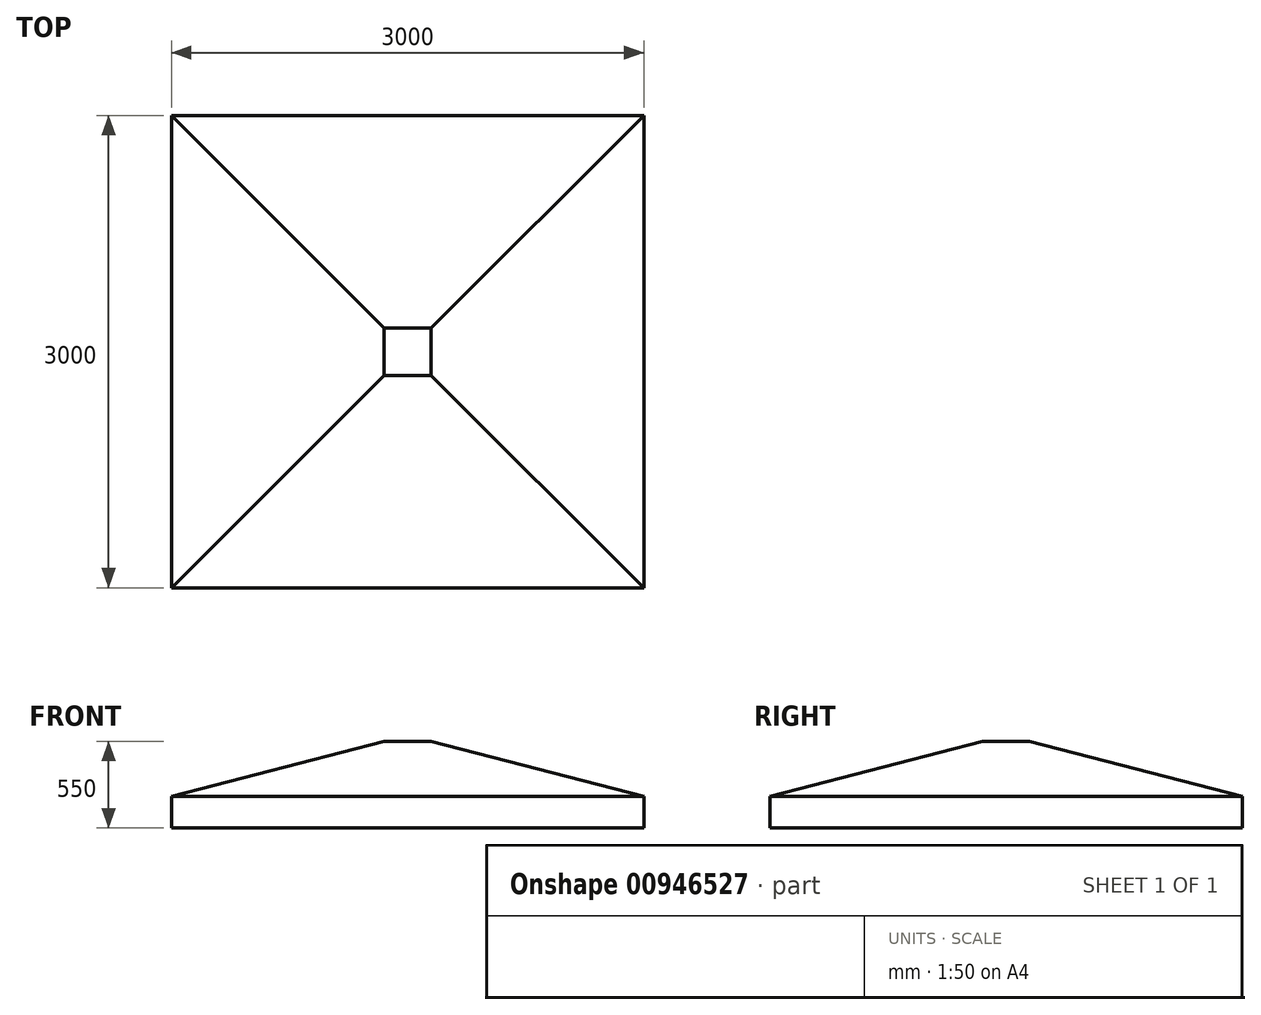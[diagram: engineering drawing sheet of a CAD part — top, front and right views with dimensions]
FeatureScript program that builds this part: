
annotation { "Feature Type Name" : "Feature", "Feature Type Description" : "" }
export const myFeature = defineFeature(function(context is Context, id is Id, definition is map)
    precondition{}
    {
        {
            var Q0;
            Q0=qCreatedBy(makeId("Top.planeOp"),FACE);
            cPlane(context, id + "F0", {"entities" : qUnion([Q0]), "cplaneType" : CPlaneType.OFFSET, "offset" : 350 * mm, "width" : 150 * mm, "height" : 150 * mm});
        }
        {
            var Q0;
            Q0=qCreatedBy(id+"F0.planeOp",FACE);
            var sketch = newSketch(context, id + "F1", { "sketchPlane" : qUnion([Q0])});
            skLineSegment(sketch, "E0.bottom", {"start": v(150, -150) * mm, "end": v(-150, -150) * mm});
            skLineSegment(sketch, "E0.top", {"start": v(150, 150) * mm, "end": v(-150, 150) * mm});
            skLineSegment(sketch, "E0.left", {"start": v(150, -150) * mm, "end": v(150, 150) * mm});
            skLineSegment(sketch, "E0.right", {"start": v(-150, -150) * mm, "end": v(-150, 150) * mm});
            skPoint(sketch, "E0.middle", {"position": v(0, 0) * mm});
            skSolve(sketch);
        }
        {
            var Q0;
            Q0=qCreatedBy(makeId("Top.planeOp"),FACE);
            var sketch = newSketch(context, id + "F2", { "sketchPlane" : qUnion([Q0])});
            skLineSegment(sketch, "E1.bottom", {"start": v(1500, -1500) * mm, "end": v(-1500, -1500) * mm});
            skLineSegment(sketch, "E1.top", {"start": v(1500, 1500) * mm, "end": v(-1500, 1500) * mm});
            skLineSegment(sketch, "E1.left", {"start": v(1500, -1500) * mm, "end": v(1500, 1500) * mm});
            skLineSegment(sketch, "E1.right", {"start": v(-1500, -1500) * mm, "end": v(-1500, 1500) * mm});
            skPoint(sketch, "E1.middle", {"position": v(0, 0) * mm});
            skSolve(sketch);
        }
        {
            var Q0;
            Q0=makeQuery(id+"F1.imprint","IMPRINT",FACE,{"disambiguationData":[TD([[makeQuery(id+"F1.imprint","IMPRINT",EDGE,{"derivedFrom":sQuery(id+"F1.wireOp",EDGE,"E0.bottom")}),-1.0]])]});
            var Q1;
            Q1=makeQuery(id+"F2.imprint","IMPRINT",FACE,{"disambiguationData":[TD([[makeQuery(id+"F2.imprint","IMPRINT",EDGE,{"derivedFrom":sQuery(id+"F2.wireOp",EDGE,"E1.bottom")}),-1.0]])]});
            loft(context, id + "F3", {"sheetProfilesArray" : [{ "sheetProfileEntities" : qUnion([Q0]) }, { "sheetProfileEntities" : qUnion([Q1]) }]});
        }
        {
            var Q0;
            Q0=qCreatedBy(makeId("Top.planeOp"),FACE);
            var sketch = newSketch(context, id + "F4", { "sketchPlane" : qUnion([Q0])});
            skLineSegment(sketch, "E2.bottom", {"start": v(1500, -1500) * mm, "end": v(-1500, -1500) * mm});
            skLineSegment(sketch, "E2.top", {"start": v(1500, 1500) * mm, "end": v(-1500, 1500) * mm});
            skLineSegment(sketch, "E2.left", {"start": v(1500, -1500) * mm, "end": v(1500, 1500) * mm});
            skLineSegment(sketch, "E2.right", {"start": v(-1500, -1500) * mm, "end": v(-1500, 1500) * mm});
            skPoint(sketch, "E2.middle", {"position": v(0, 0) * mm});
            skSolve(sketch);
        }
        {
            var Q0;
            Q0 = qSketchRegion(id + "F4", true);
            extrude(context, id + "F5", {"entities" : qUnion([Q0]), "operationType" : NewBodyOperationType.ADD, "oppositeDirection" : true, "depth" : 200 * mm, "offsetDistance" : 25 * mm});
        }
        {
            var Q0;
            Q0=makeQuery(id+"F5.opExtrude","CAP_FACE",FACE,{"disambiguationData":[OSD([sQuery(id+"F4.wireOp",EDGE,"E2.bottom"),sQuery(id+"F4.wireOp",EDGE,"E2.top"),sQuery(id+"F4.wireOp",EDGE,"E2.left"),sQuery(id+"F4.wireOp",EDGE,"E2.right")])],"isStart":false});
            shell(context, id + "F6", {"entities" : qUnion([Q0]), "thickness" : 2.5 * mm});
        }
    });
